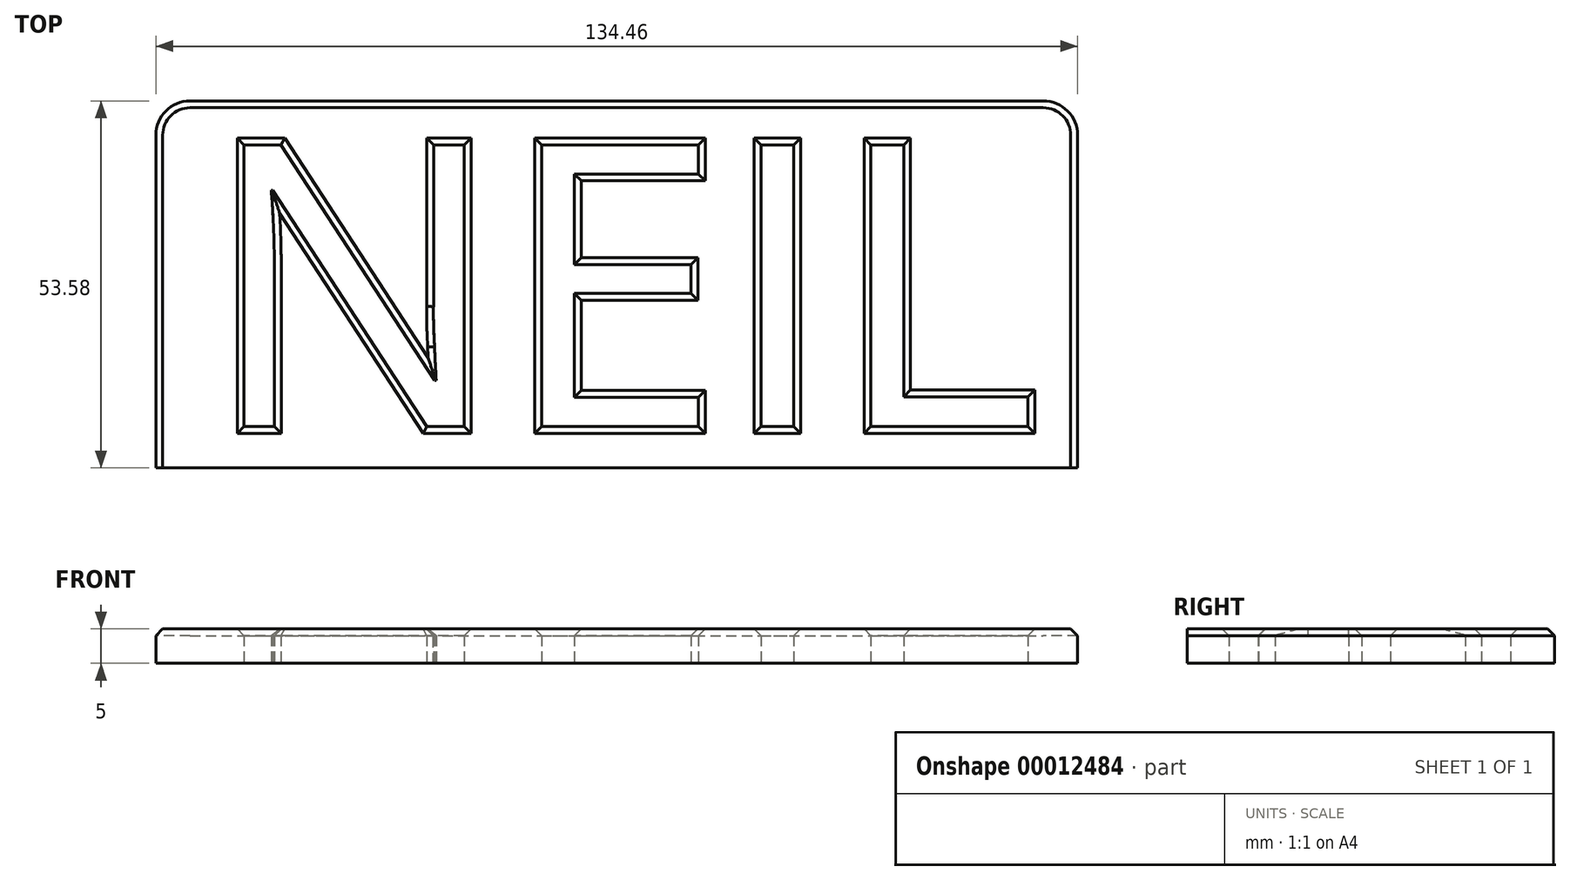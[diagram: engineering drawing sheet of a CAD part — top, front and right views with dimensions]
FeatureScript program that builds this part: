
annotation { "Feature Type Name" : "Feature", "Feature Type Description" : "" }
export const myFeature = defineFeature(function(context is Context, id is Id, definition is map)
    precondition{}
    {
        {
            var Q0;
            Q0=qCreatedBy(makeId("Top.planeOp"),FACE);
            var sketch = newSketch(context, id + "F0", { "sketchPlane" : qUnion([Q0])});
            skLineSegment(sketch, "E0.rect.bottom", {"start": v(60, -20.72) * mm, "end": v(-60, -20.72) * mm, "construction": true});
            skLineSegment(sketch, "E0.rect.top", {"start": v(60, 20.72) * mm, "end": v(-60, 20.72) * mm, "construction": true});
            skLineSegment(sketch, "E0.rect.left", {"start": v(60, -20.72) * mm, "end": v(60, 20.72) * mm, "construction": true});
            skLineSegment(sketch, "E0.rect.right", {"start": v(-60, -20.72) * mm, "end": v(-60, 20.72) * mm, "construction": true});
            skPoint(sketch, "E0.rect.middle", {"position": v(0, 0) * mm});
            skText(sketch, "E1", { "text": "NEIL\n", "fontName": "OpenSans-Regular.ttf"});
            skLineSegment(sketch, "E2.rect.bottom", {"start": v(67.23, -26.79) * mm, "end": v(-67.23, -26.79) * mm});
            skLineSegment(sketch, "E2.rect.top", {"start": v(67.23, 26.79) * mm, "end": v(-67.23, 26.79) * mm});
            skLineSegment(sketch, "E2.rect.left", {"start": v(67.23, -26.79) * mm, "end": v(67.23, 26.79) * mm});
            skLineSegment(sketch, "E2.rect.right", {"start": v(-67.23, -26.79) * mm, "end": v(-67.23, 26.79) * mm});
            const initialGuessF0  = {"E1": [-0.06, -0.02072, 1, 0, 0.04144]};
            skSetInitialGuess(sketch, initialGuessF0);
            skSolve(sketch);
        }
        {
            var Q0;
            Q0=makeQuery(id+"F0.imprint","IMPRINT",FACE,{"disambiguationData":[TD([[makeQuery(id+"F0.imprint","IMPRINT",EDGE,{"derivedFrom":sQuery(id+"F0.wireOp",EDGE,"E1.sketch_text.stroke-0")}),1.0]])]});
            extrude(context, id + "F1", {"entities" : qUnion([Q0]), "depth" : 5 * mm});
        }
        {
            var Q0;
            Q0=makeQuery(id+"F0.imprint","IMPRINT",FACE,{"disambiguationData":[TD([[makeQuery(id+"F0.imprint","IMPRINT",EDGE,{"derivedFrom":sQuery(id+"F0.wireOp",EDGE,"E1.sketch_text.stroke-0")}),-1.0]])]});
            var Q1;
            Q1=makeQuery(id+"F0.imprint","IMPRINT",FACE,{"disambiguationData":[TD([[makeQuery(id+"F0.imprint","IMPRINT",EDGE,{"derivedFrom":sQuery(id+"F0.wireOp",EDGE,"E1.sketch_text.stroke-15")}),-1.0]])]});
            var Q2;
            Q2=makeQuery(id+"F0.imprint","IMPRINT",FACE,{"disambiguationData":[TD([[makeQuery(id+"F0.imprint","IMPRINT",EDGE,{"derivedFrom":sQuery(id+"F0.wireOp",EDGE,"E1.sketch_text.stroke-27")}),-1.0]])]});
            var Q3;
            Q3=makeQuery(id+"F0.imprint","IMPRINT",FACE,{"disambiguationData":[TD([[makeQuery(id+"F0.imprint","IMPRINT",EDGE,{"derivedFrom":sQuery(id+"F0.wireOp",EDGE,"E1.sketch_text.stroke-31")}),-1.0]])]});
            extrude(context, id + "F2", {"entities" : qUnion([Q0, Q1, Q2, Q3]), "operationType" : NewBodyOperationType.REMOVE, "oppositeDirection" : true, "depth" : 25 * mm, "hasSecondDirection" : true, "secondDirectionOppositeDirection" : false, "secondDirectionDepth" : 25 * mm});
        }
        {
            var Q0;
            Q0=makeQuery(id+"F1.opExtrude","SWEPT_EDGE",EDGE,{"disambiguationData":[OSD([sQuery(id+"F0.wireOp",EDGE,"E2.rect.top"),sQuery(id+"F0.wireOp",EDGE,"E2.rect.left")])]});
            var Q1;
            Q1=makeQuery(id+"F1.opExtrude","SWEPT_EDGE",EDGE,{"disambiguationData":[OSD([sQuery(id+"F0.wireOp",EDGE,"E2.rect.top"),sQuery(id+"F0.wireOp",EDGE,"E2.rect.right")])]});
            fillet(context, id + "F3", {"entities" : qUnion([Q0, Q1]), "radius" : 5 * mm, "tangentPropagation" : true, "allowEdgeOverflow" : false});
        }
        {
            var Q0;
            Q0=makeQuery(id+"F1.opExtrude","CAP_EDGE",EDGE,{"disambiguationData":[OSD([sQuery(id+"F0.wireOp",EDGE,"E2.rect.top")])],"isStart":false});
            var Q1;
            Q1=makeQuery(id+"F1.opExtrude","CAP_EDGE",EDGE,{"disambiguationData":[OSD([sQuery(id+"F0.wireOp",EDGE,"E1.sketch_text.stroke-6")])],"isStart":false});
            var Q2;
            Q2=makeQuery(id+"F1.opExtrude","CAP_EDGE",EDGE,{"disambiguationData":[OSD([sQuery(id+"F0.wireOp",EDGE,"E1.sketch_text.stroke-7")])],"isStart":false});
            var Q3;
            Q3=makeQuery(id+"F1.opExtrude","CAP_EDGE",EDGE,{"disambiguationData":[OSD([sQuery(id+"F0.wireOp",EDGE,"E1.sketch_text.stroke-8")])],"isStart":false});
            var Q4;
            Q4=makeQuery(id+"F1.opExtrude","CAP_EDGE",EDGE,{"disambiguationData":[OSD([sQuery(id+"F0.wireOp",EDGE,"E1.sketch_text.stroke-12")])],"isStart":false});
            var Q5;
            Q5=makeQuery(id+"F1.opExtrude","CAP_EDGE",EDGE,{"disambiguationData":[OSD([sQuery(id+"F0.wireOp",EDGE,"E1.sketch_text.stroke-11")])],"isStart":false});
            var Q6;
            Q6=makeQuery(id+"F1.opExtrude","CAP_EDGE",EDGE,{"disambiguationData":[OSD([sQuery(id+"F0.wireOp",EDGE,"E1.sketch_text.stroke-10")])],"isStart":false});
            var Q7;
            Q7=makeQuery(id+"F1.opExtrude","CAP_EDGE",EDGE,{"disambiguationData":[OSD([sQuery(id+"F0.wireOp",EDGE,"E1.sketch_text.stroke-14")])],"isStart":false});
            var Q8;
            Q8=makeQuery(id+"F1.opExtrude","CAP_EDGE",EDGE,{"disambiguationData":[OSD([sQuery(id+"F0.wireOp",EDGE,"E1.sketch_text.stroke-13")])],"isStart":false});
            var Q9;
            Q9=makeQuery(id+"F1.opExtrude","CAP_EDGE",EDGE,{"disambiguationData":[OSD([sQuery(id+"F0.wireOp",EDGE,"E1.sketch_text.stroke-0")])],"isStart":false});
            var Q10;
            Q10=makeQuery(id+"F1.opExtrude","CAP_EDGE",EDGE,{"disambiguationData":[OSD([sQuery(id+"F0.wireOp",EDGE,"E1.sketch_text.stroke-1")])],"isStart":false});
            var Q11;
            Q11=makeQuery(id+"F1.opExtrude","CAP_EDGE",EDGE,{"disambiguationData":[OSD([sQuery(id+"F0.wireOp",EDGE,"E1.sketch_text.stroke-4")])],"isStart":false});
            var Q12;
            Q12=makeQuery(id+"F1.opExtrude","CAP_EDGE",EDGE,{"disambiguationData":[OSD([sQuery(id+"F0.wireOp",EDGE,"E1.sketch_text.stroke-3")])],"isStart":false});
            var Q13;
            Q13=makeQuery(id+"F1.opExtrude","CAP_EDGE",EDGE,{"disambiguationData":[OSD([sQuery(id+"F0.wireOp",EDGE,"E1.sketch_text.stroke-5")])],"isStart":false});
            var Q14;
            Q14=makeQuery(id+"F1.opExtrude","CAP_EDGE",EDGE,{"disambiguationData":[OSD([sQuery(id+"F0.wireOp",EDGE,"E1.sketch_text.stroke-17")])],"isStart":false});
            var Q15;
            Q15=makeQuery(id+"F1.opExtrude","CAP_EDGE",EDGE,{"disambiguationData":[OSD([sQuery(id+"F0.wireOp",EDGE,"E1.sketch_text.stroke-18")])],"isStart":false});
            var Q16;
            Q16=makeQuery(id+"F1.opExtrude","CAP_EDGE",EDGE,{"disambiguationData":[OSD([sQuery(id+"F0.wireOp",EDGE,"E1.sketch_text.stroke-19")])],"isStart":false});
            var Q17;
            Q17=makeQuery(id+"F1.opExtrude","CAP_EDGE",EDGE,{"disambiguationData":[OSD([sQuery(id+"F0.wireOp",EDGE,"E1.sketch_text.stroke-16")])],"isStart":false});
            var Q18;
            Q18=makeQuery(id+"F1.opExtrude","CAP_EDGE",EDGE,{"disambiguationData":[OSD([sQuery(id+"F0.wireOp",EDGE,"E1.sketch_text.stroke-20")])],"isStart":false});
            var Q19;
            Q19=makeQuery(id+"F1.opExtrude","CAP_EDGE",EDGE,{"disambiguationData":[OSD([sQuery(id+"F0.wireOp",EDGE,"E1.sketch_text.stroke-21")])],"isStart":false});
            var Q20;
            Q20=makeQuery(id+"F1.opExtrude","CAP_EDGE",EDGE,{"disambiguationData":[OSD([sQuery(id+"F0.wireOp",EDGE,"E1.sketch_text.stroke-22")])],"isStart":false});
            var Q21;
            Q21=makeQuery(id+"F1.opExtrude","CAP_EDGE",EDGE,{"disambiguationData":[OSD([sQuery(id+"F0.wireOp",EDGE,"E1.sketch_text.stroke-23")])],"isStart":false});
            var Q22;
            Q22=makeQuery(id+"F1.opExtrude","CAP_EDGE",EDGE,{"disambiguationData":[OSD([sQuery(id+"F0.wireOp",EDGE,"E1.sketch_text.stroke-24")])],"isStart":false});
            var Q23;
            Q23=makeQuery(id+"F1.opExtrude","CAP_EDGE",EDGE,{"disambiguationData":[OSD([sQuery(id+"F0.wireOp",EDGE,"E1.sketch_text.stroke-25")])],"isStart":false});
            var Q24;
            Q24=makeQuery(id+"F1.opExtrude","CAP_EDGE",EDGE,{"disambiguationData":[OSD([sQuery(id+"F0.wireOp",EDGE,"E1.sketch_text.stroke-26")])],"isStart":false});
            var Q25;
            Q25=makeQuery(id+"F1.opExtrude","CAP_EDGE",EDGE,{"disambiguationData":[OSD([sQuery(id+"F0.wireOp",EDGE,"E1.sketch_text.stroke-15")])],"isStart":false});
            var Q26;
            Q26=makeQuery(id+"F1.opExtrude","CAP_EDGE",EDGE,{"disambiguationData":[OSD([sQuery(id+"F0.wireOp",EDGE,"E1.sketch_text.stroke-27")])],"isStart":false});
            var Q27;
            Q27=makeQuery(id+"F1.opExtrude","CAP_EDGE",EDGE,{"disambiguationData":[OSD([sQuery(id+"F0.wireOp",EDGE,"E1.sketch_text.stroke-28")])],"isStart":false});
            var Q28;
            Q28=makeQuery(id+"F1.opExtrude","CAP_EDGE",EDGE,{"disambiguationData":[OSD([sQuery(id+"F0.wireOp",EDGE,"E1.sketch_text.stroke-29")])],"isStart":false});
            var Q29;
            Q29=makeQuery(id+"F1.opExtrude","CAP_EDGE",EDGE,{"disambiguationData":[OSD([sQuery(id+"F0.wireOp",EDGE,"E1.sketch_text.stroke-30")])],"isStart":false});
            var Q30;
            Q30=makeQuery(id+"F1.opExtrude","CAP_EDGE",EDGE,{"disambiguationData":[OSD([sQuery(id+"F0.wireOp",EDGE,"E1.sketch_text.stroke-36")])],"isStart":false});
            var Q31;
            Q31=makeQuery(id+"F1.opExtrude","CAP_EDGE",EDGE,{"disambiguationData":[OSD([sQuery(id+"F0.wireOp",EDGE,"E1.sketch_text.stroke-31")])],"isStart":false});
            var Q32;
            Q32=makeQuery(id+"F1.opExtrude","CAP_EDGE",EDGE,{"disambiguationData":[OSD([sQuery(id+"F0.wireOp",EDGE,"E1.sketch_text.stroke-32")])],"isStart":false});
            var Q33;
            Q33=makeQuery(id+"F1.opExtrude","CAP_EDGE",EDGE,{"disambiguationData":[OSD([sQuery(id+"F0.wireOp",EDGE,"E1.sketch_text.stroke-33")])],"isStart":false});
            var Q34;
            Q34=makeQuery(id+"F1.opExtrude","CAP_EDGE",EDGE,{"disambiguationData":[OSD([sQuery(id+"F0.wireOp",EDGE,"E1.sketch_text.stroke-34")])],"isStart":false});
            var Q35;
            Q35=makeQuery(id+"F1.opExtrude","CAP_EDGE",EDGE,{"disambiguationData":[OSD([sQuery(id+"F0.wireOp",EDGE,"E1.sketch_text.stroke-35")])],"isStart":false});
            chamfer(context, id + "F4", {"entities" : qUnion([Q0, Q1, Q2, Q3, Q4, Q5, Q6, Q7, Q8, Q9, Q10, Q11, Q12, Q13, Q14, Q15, Q16, Q17, Q18, Q19, Q20, Q21, Q22, Q23, Q24, Q25, Q26, Q27, Q28, Q29, Q30, Q31, Q32, Q33, Q34, Q35]), "width" : 1 * mm, "tangentPropagation" : true});
        }
    });
